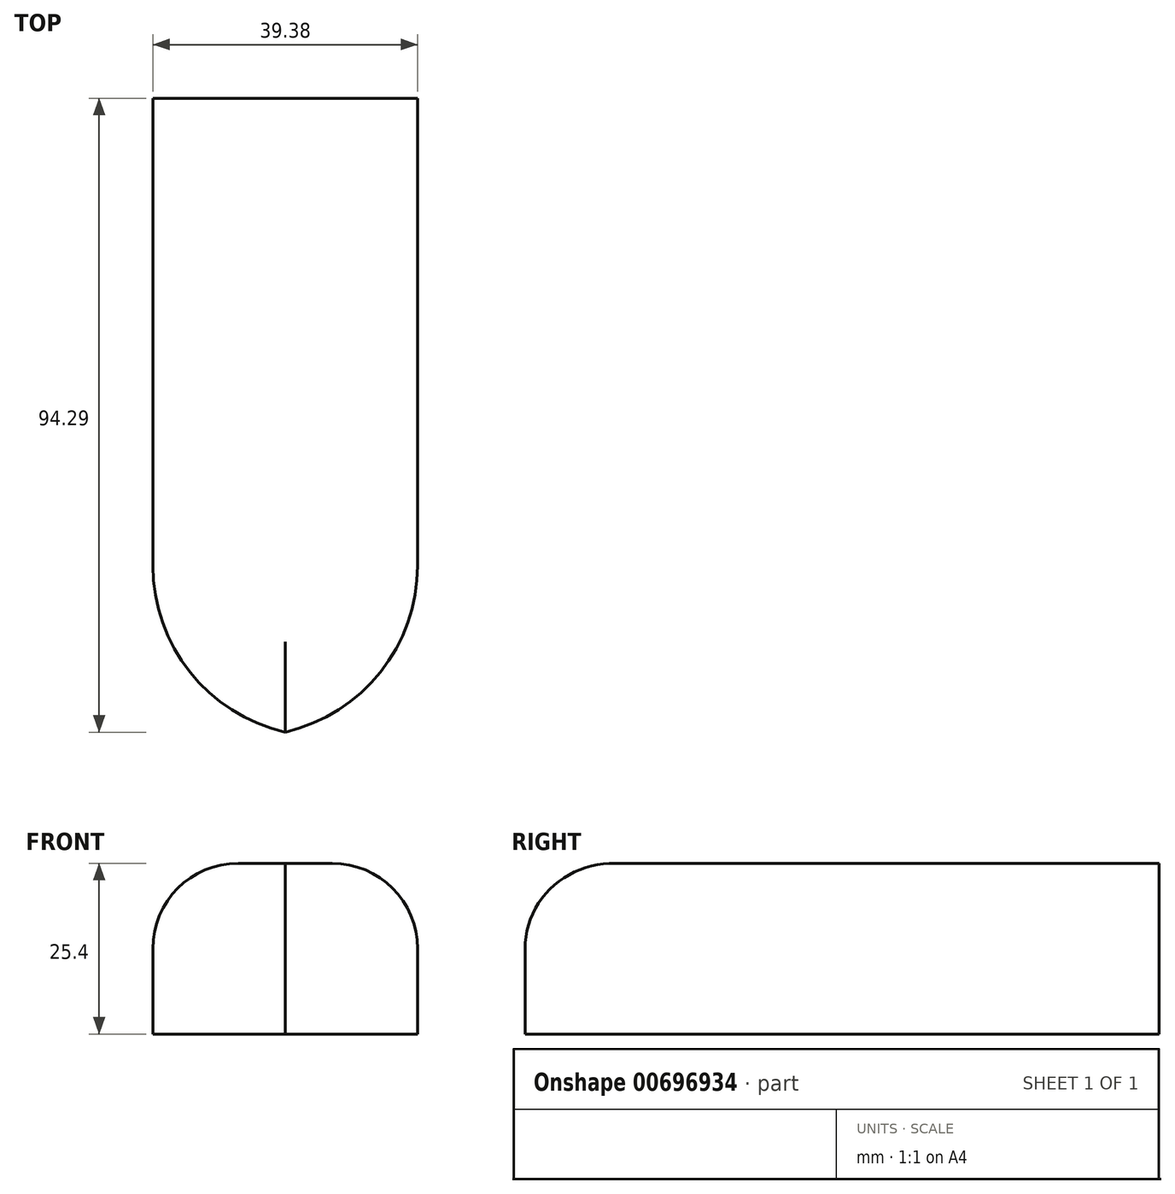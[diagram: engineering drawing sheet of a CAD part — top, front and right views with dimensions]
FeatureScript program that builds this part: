
annotation { "Feature Type Name" : "Feature", "Feature Type Description" : "" }
export const myFeature = defineFeature(function(context is Context, id is Id, definition is map)
    precondition{}
    {
        {
            var Q0;
            Q0=qCreatedBy(makeId("Top.planeOp"),FACE);
            var sketch = newSketch(context, id + "F0", { "sketchPlane" : qUnion([Q0])});
            skLineSegment(sketch, "E0.bottom", {"start": v(19.7, -47.47) * mm, "end": v(-19.7, -47.47) * mm});
            skLineSegment(sketch, "E0.top", {"start": v(19.7, 47.47) * mm, "end": v(-19.7, 47.47) * mm});
            skLineSegment(sketch, "E0.left", {"start": v(19.7, -47.47) * mm, "end": v(19.7, 47.47) * mm});
            skLineSegment(sketch, "E0.right", {"start": v(-19.7, -47.47) * mm, "end": v(-19.7, 47.47) * mm});
            skPoint(sketch, "E0.middle", {"position": v(0, 0) * mm});
            skSolve(sketch);
        }
        {
            var Q0;
            Q0=makeQuery(id+"F0.imprint","IMPRINT",FACE,{"disambiguationData":[TD([[makeQuery(id+"F0.imprint","IMPRINT",EDGE,{"derivedFrom":sQuery(id+"F0.wireOp",EDGE,"E0.bottom")}),-1.0]])]});
            extrude(context, id + "F1", {"entities" : qUnion([Q0]), "depth" : 25.4 * mm, "offsetDistance" : 25.4 * mm});
        }
        {
            var Q0;
            Q0=makeQuery(id+"F1.opExtrude","SWEPT_EDGE",EDGE,{"disambiguationData":[OSD([sQuery(id+"F0.wireOp",EDGE,"E0.bottom"),sQuery(id+"F0.wireOp",EDGE,"E0.left")])]});
            var Q1;
            Q1=makeQuery(id+"F1.opExtrude","SWEPT_EDGE",EDGE,{"disambiguationData":[OSD([sQuery(id+"F0.wireOp",EDGE,"E0.bottom"),sQuery(id+"F0.wireOp",EDGE,"E0.right")])]});
            fillet(context, id + "F2", {"entities" : qUnion([Q0, Q1]), "radius" : 25.4 * mm, "tangentPropagation" : true, "allowEdgeOverflow" : false});
        }
        {
            var Q0;
            Q0=makeQuery(id+"F1.opExtrude","CAP_EDGE",EDGE,{"disambiguationData":[OSD([sQuery(id+"F0.wireOp",EDGE,"E0.left")])],"isStart":false});
            var Q1;
            {var subQ0=sQuery(id+"F0.wireOp",EDGE,"E0.left");var subQ1=sQuery(id+"F0.wireOp",EDGE,"E0.bottom");Q1=makeQuery(id+"F2.opFillet","BLEND_EDGE",EDGE,{"blendedFrom":[makeQuery(id+"F1.opExtrude","SWEPT_EDGE",EDGE,{"disambiguationData":[OSD([subQ1,subQ0])]}),makeQuery(id+"F1.opExtrude","CAP_FACE",FACE,{"disambiguationData":[OSD([subQ1,sQuery(id+"F0.wireOp",EDGE,"E0.top"),subQ0,sQuery(id+"F0.wireOp",EDGE,"E0.right")])],"isStart":false})],"blendedInto":[makeQuery(id+"F1.opExtrude","CAP_FACE",FACE,{"disambiguationData":[OSD([subQ1,sQuery(id+"F0.wireOp",EDGE,"E0.top"),subQ0,sQuery(id+"F0.wireOp",EDGE,"E0.right")])],"isStart":false})]});}
            var Q2;
            {var subQ0=sQuery(id+"F0.wireOp",EDGE,"E0.right");var subQ1=sQuery(id+"F0.wireOp",EDGE,"E0.bottom");Q2=makeQuery(id+"F2.opFillet","BLEND_EDGE",EDGE,{"blendedFrom":[makeQuery(id+"F1.opExtrude","SWEPT_EDGE",EDGE,{"disambiguationData":[OSD([subQ1,subQ0])]}),makeQuery(id+"F1.opExtrude","CAP_FACE",FACE,{"disambiguationData":[OSD([subQ1,sQuery(id+"F0.wireOp",EDGE,"E0.top"),sQuery(id+"F0.wireOp",EDGE,"E0.left"),subQ0])],"isStart":false})],"blendedInto":[makeQuery(id+"F1.opExtrude","CAP_FACE",FACE,{"disambiguationData":[OSD([subQ1,sQuery(id+"F0.wireOp",EDGE,"E0.top"),sQuery(id+"F0.wireOp",EDGE,"E0.left"),subQ0])],"isStart":false})]});}
            var Q3;
            Q3=makeQuery(id+"F1.opExtrude","CAP_EDGE",EDGE,{"disambiguationData":[OSD([sQuery(id+"F0.wireOp",EDGE,"E0.right")])],"isStart":false});
            fillet(context, id + "F3", {"entities" : qUnion([Q0, Q1, Q2, Q3]), "radius" : 12.7 * mm, "tangentPropagation" : true, "allowEdgeOverflow" : false});
        }
    });
